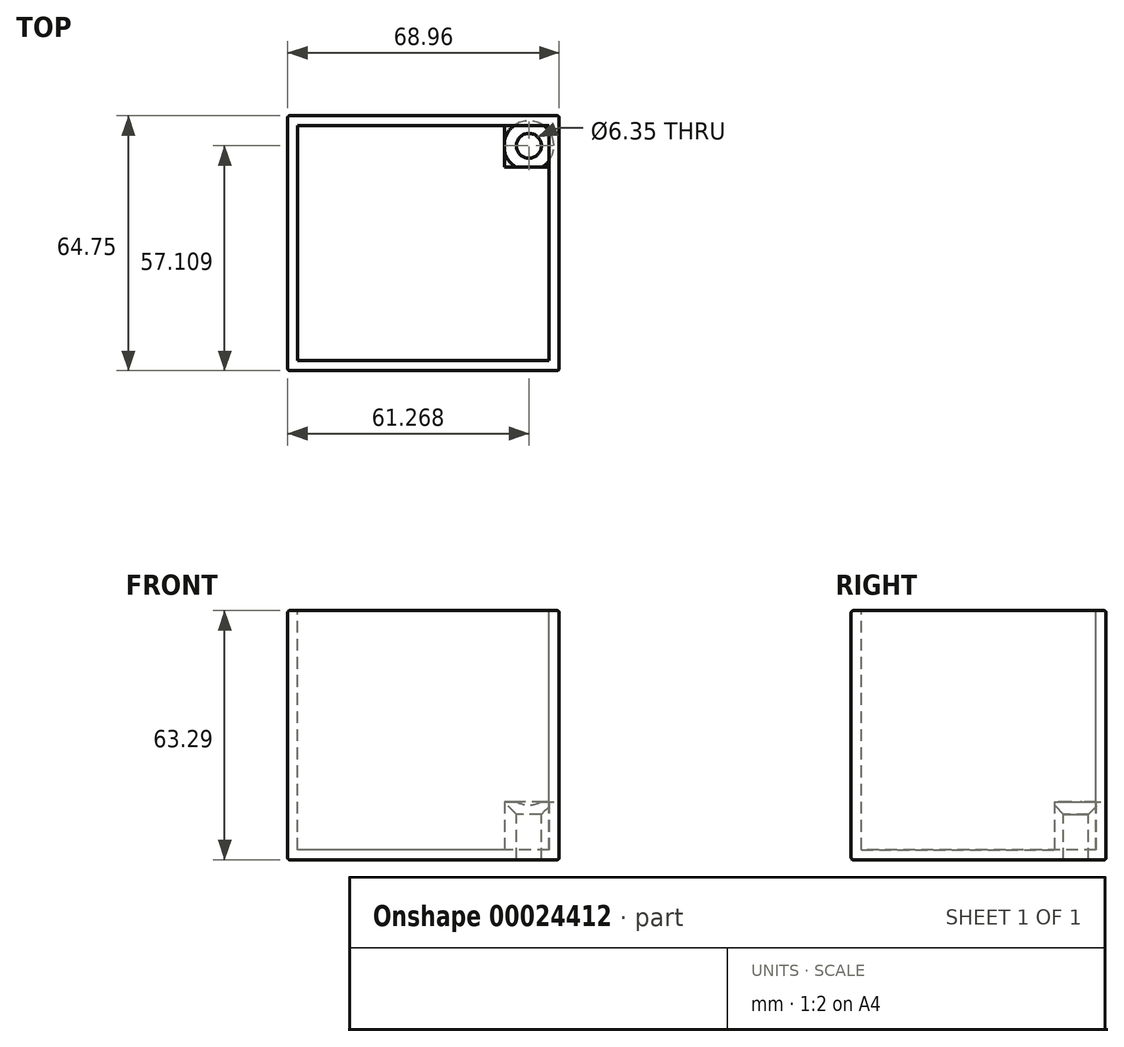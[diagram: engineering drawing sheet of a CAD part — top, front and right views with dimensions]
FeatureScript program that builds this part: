
annotation { "Feature Type Name" : "Feature", "Feature Type Description" : "" }
export const myFeature = defineFeature(function(context is Context, id is Id, definition is map)
    precondition{}
    {
        {
            var Q0;
            Q0=qCreatedBy(makeId("Top.planeOp"),FACE);
            var sketch = newSketch(context, id + "F0", { "sketchPlane" : qUnion([Q0])});
            skLineSegment(sketch, "E0.bottom", {"start": v(-125.85, 54.98) * mm, "end": v(-56.9, 54.98) * mm});
            skLineSegment(sketch, "E0.top", {"start": v(-125.85, -9.77) * mm, "end": v(-56.9, -9.77) * mm});
            skLineSegment(sketch, "E0.left", {"start": v(-125.85, 54.98) * mm, "end": v(-125.85, -9.77) * mm});
            skLineSegment(sketch, "E0.right", {"start": v(-56.9, 54.98) * mm, "end": v(-56.9, -9.77) * mm});
            skSolve(sketch);
        }
        {
            var Q0;
            Q0=makeQuery(id+"F0.imprint","IMPRINT",FACE,{"disambiguationData":[TD([[makeQuery(id+"F0.imprint","IMPRINT",EDGE,{"derivedFrom":sQuery(id+"F0.wireOp",EDGE,"E0.bottom")}),-1.0]])]});
            extrude(context, id + "F1", {"entities" : qUnion([Q0]), "depth" : 63.3 * mm});
        }
        {
            var Q0;
            Q0=makeQuery(id+"F1.opExtrude","CAP_EDGE",EDGE,{"disambiguationData":[OSD([sQuery(id+"F0.wireOp",EDGE,"E0.left")])],"isStart":true});
            var Q1;
            Q1=makeQuery(id+"F1.opExtrude","CAP_EDGE",EDGE,{"disambiguationData":[OSD([sQuery(id+"F0.wireOp",EDGE,"E0.left")])],"isStart":false});
            var Q2;
            Q2=makeQuery(id+"F1.opExtrude","CAP_EDGE",EDGE,{"disambiguationData":[OSD([sQuery(id+"F0.wireOp",EDGE,"E0.right")])],"isStart":false});
            var Q3;
            Q3=makeQuery(id+"F1.opExtrude","CAP_EDGE",EDGE,{"disambiguationData":[OSD([sQuery(id+"F0.wireOp",EDGE,"E0.top")])],"isStart":false});
            var Q4;
            Q4=makeQuery(id+"F1.opExtrude","SWEPT_FACE",FACE,{"disambiguationData":[OSD([sQuery(id+"F0.wireOp",EDGE,"E0.left")])]});
            var Q5;
            Q5=makeQuery(id+"F1.opExtrude","SWEPT_EDGE",EDGE,{"disambiguationData":[OSD([sQuery(id+"F0.wireOp",EDGE,"E0.top"),sQuery(id+"F0.wireOp",EDGE,"E0.right")])]});
            var Q6;
            Q6=makeQuery(id+"F1.opExtrude","SWEPT_FACE",FACE,{"disambiguationData":[OSD([sQuery(id+"F0.wireOp",EDGE,"E0.top")])]});
            var Q7;
            Q7=makeQuery(id+"F1.opExtrude","SWEPT_EDGE",EDGE,{"disambiguationData":[OSD([sQuery(id+"F0.wireOp",EDGE,"E0.top"),sQuery(id+"F0.wireOp",EDGE,"E0.left")])]});
            var Q8;
            Q8=makeQuery(id+"F1.opExtrude","CAP_FACE",FACE,{"disambiguationData":[OSD([sQuery(id+"F0.wireOp",EDGE,"E0.bottom"),sQuery(id+"F0.wireOp",EDGE,"E0.top"),sQuery(id+"F0.wireOp",EDGE,"E0.left"),sQuery(id+"F0.wireOp",EDGE,"E0.right")])],"isStart":false});
            var Q9;
            Q9=makeQuery(id+"F1.opExtrude","SWEPT_EDGE",EDGE,{"disambiguationData":[OSD([sQuery(id+"F0.wireOp",EDGE,"E0.bottom"),sQuery(id+"F0.wireOp",EDGE,"E0.left")])]});
            var Q10;
            Q10=makeQuery(id+"F1.opExtrude","SWEPT_FACE",FACE,{"disambiguationData":[OSD([sQuery(id+"F0.wireOp",EDGE,"E0.bottom")])]});
            var Q11;
            Q11=makeQuery(id+"F1.opExtrude","CAP_EDGE",EDGE,{"disambiguationData":[OSD([sQuery(id+"F0.wireOp",EDGE,"E0.top")])],"isStart":true});
            var Q12;
            Q12=makeQuery(id+"F1.opExtrude","CAP_EDGE",EDGE,{"disambiguationData":[OSD([sQuery(id+"F0.wireOp",EDGE,"E0.right")])],"isStart":true});
            var Q13;
            Q13=makeQuery(id+"F1.opExtrude","CAP_EDGE",EDGE,{"disambiguationData":[OSD([sQuery(id+"F0.wireOp",EDGE,"E0.bottom")])],"isStart":false});
            var Q14;
            Q14=makeQuery(id+"F1.opExtrude","SWEPT_FACE",FACE,{"disambiguationData":[OSD([sQuery(id+"F0.wireOp",EDGE,"E0.right")])]});
            var Q15;
            Q15=makeQuery(id+"F1.opExtrude","CAP_EDGE",EDGE,{"disambiguationData":[OSD([sQuery(id+"F0.wireOp",EDGE,"E0.bottom")])],"isStart":true});
            var Q16;
            Q16=makeQuery(id+"F1.opExtrude","SWEPT_EDGE",EDGE,{"disambiguationData":[OSD([sQuery(id+"F0.wireOp",EDGE,"E0.bottom"),sQuery(id+"F0.wireOp",EDGE,"E0.right")])]});
            var Q17;
            Q17=makeQuery(id+"F1.opExtrude","CAP_FACE",FACE,{"disambiguationData":[OSD([sQuery(id+"F0.wireOp",EDGE,"E0.bottom"),sQuery(id+"F0.wireOp",EDGE,"E0.top"),sQuery(id+"F0.wireOp",EDGE,"E0.left"),sQuery(id+"F0.wireOp",EDGE,"E0.right")])],"isStart":true});
            fillet(context, id + "F2", {"entities" : qUnion([Q0, Q1, Q2, Q3, Q4, Q5, Q6, Q7, Q8, Q9, Q10, Q11, Q12, Q13, Q14, Q15, Q16, Q17]), "radius" : 0.5 * mm, "tangentPropagation" : true, "allowEdgeOverflow" : false});
        }
        {
            var Q0;
            Q0=makeQuery(id+"F1.opExtrude","CAP_FACE",FACE,{"disambiguationData":[OSD([sQuery(id+"F0.wireOp",EDGE,"E0.bottom"),sQuery(id+"F0.wireOp",EDGE,"E0.top"),sQuery(id+"F0.wireOp",EDGE,"E0.left"),sQuery(id+"F0.wireOp",EDGE,"E0.right")])],"isStart":false});
            shell(context, id + "F3", {"entities" : qUnion([Q0]), "thickness" : 2.54 * mm});
        }
        {
            var Q0;
            Q0=makeQuery(id+"F3.opShell","OFFSET_FACE",FACE,{"disambiguationData":[OSD([sQuery(id+"F0.wireOp",EDGE,"E0.bottom"),sQuery(id+"F0.wireOp",EDGE,"E0.top"),sQuery(id+"F0.wireOp",EDGE,"E0.left"),sQuery(id+"F0.wireOp",EDGE,"E0.right")])]});
            var sketch = newSketch(context, id + "F4", { "sketchPlane" : qUnion([Q0])});
            skLineSegment(sketch, "E1", {"start": v(-70.76, 52.44) * mm, "end": v(-70.76, 41.9) * mm});
            skLineSegment(sketch, "E2", {"start": v(-59.43, 41.9) * mm, "end": v(-70.76, 41.9) * mm});
            skSolve(sketch);
        }
        {
            var Q0;
            {var subQ11=sQuery(id+"F4.wireOp",EDGE,"E1");Q0=makeQuery(id+"F4.imprint","IMPRINT",FACE,{"disambiguationData":[TD([[makeQuery(id+"F4.imprint","IMPRINT",EDGE,{"derivedFrom":subQ11}),1.0]])]});}
            extrude(context, id + "F5", {"entities" : qUnion([Q0]), "operationType" : NewBodyOperationType.ADD, "depth" : 12.2 * mm});
        }
        {
            var Q0;
            Q0=makeQuery(id+"F5.opExtrude","CAP_FACE",FACE,{"disambiguationData":[OSD([sQuery(id+"F0.wireOp",EDGE,"E0.bottom"),sQuery(id+"F0.wireOp",EDGE,"E0.top"),sQuery(id+"F0.wireOp",EDGE,"E0.left"),sQuery(id+"F0.wireOp",EDGE,"E0.right"),sQuery(id+"F4.wireOp",EDGE,"E1"),sQuery(id+"F4.wireOp",EDGE,"E2")])],"isStart":false});
            var sketch = newSketch(context, id + "F6", { "sketchPlane" : qUnion([Q0])});
            skPoint(sketch, "E3", {"position": v(-64.58, 47.34) * mm});
            skSolve(sketch);
        }
        {
            var Q0;
            Q0=sQuery(id+"F6.wireOp",VERTEX,"E3");
            var Q1;
            Q1=makeQuery(id+"F1.opExtrude","SWEPT_BODY",BODY,{"disambiguationData":[OSD([sQuery(id+"F0.wireOp",EDGE,"E0.bottom"),sQuery(id+"F0.wireOp",EDGE,"E0.top"),sQuery(id+"F0.wireOp",EDGE,"E0.left"),sQuery(id+"F0.wireOp",EDGE,"E0.right")])]});
            hole(context, id + "F7", {"style" : HoleStyle.C_SINK, "holeDiameter" : 6.35 * mm, "cSinkDiameter" : 12.7 * mm, "endStyle" : HoleEndStyle.THROUGH, "locations" : qUnion([Q0]), "scope" : qUnion([Q1]), "cSinkAngle" : 90 * degree});
        }
    });
